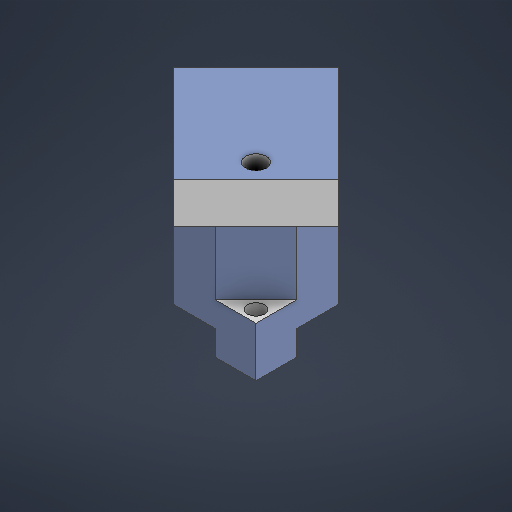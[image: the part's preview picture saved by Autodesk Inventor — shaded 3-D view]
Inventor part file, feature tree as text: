
AUTODESK INVENTOR PART (.ipt)
format: ipt  version: 2025.1 (Build 291241000, 241)  size: 527,360 bytes
history: native  units: in
note: dims shown in document units (in); Inventor stores cm internally (conversion verified against a paired STEP export)
features: extrude x10, sketch x10, projected_geometry x1, other x1
ambient origin geometry x8: Origin, YZ Plane, XZ Plane, XY Plane, X Axis, Y Axis, Z Axis, Center Point
bodies: Solid1 (feature_tree)
feature tree (22):
  extrude  "Extrusion1"  Depth=0.1949in
  extrude  "Extrusion2"  Depth=0.3937in
  extrude  "Extrusion3"  Depth=0.3937in TaperAngle=0.0deg
  extrude  "Extrusion4"  Depth=0.1969in TaperAngle=0.0deg
  extrude  "Extrusion5"  Depth=0.1969in TaperAngle=0.0deg
  extrude  "Extrusion6"  Depth=0.1299in
  extrude  "Extrusion7"  Depth=0.105in
  extrude  "Extrusion8"  Depth=0.0571in
  extrude  "Extrusion9"  Depth=0.3937in TaperAngle=0.0deg
  extrude  "Extrusion10"  Depth=0.6496in
  sketch  "Sketch1"  dims[d0=0.1949in d1=0.1949in]
  sketch  "Sketch2"  dims[d2=0.2362in d3=0.0in d4=0.3937in]
  sketch  "Sketch3"  dims[d5=0.3937in d6=0.0787in d7=0.0in]
  sketch  "Sketch4"  dims[d8=0.7776in d9=0.0in d10=0.1969in d11=0.0in]
  sketch  "Sketch6"  dims[d12=0.0984in d13=0.1969in d14=0.0in]
  sketch  "Sketch7"  dims[d15=0.0787in d16=0.0in d17=0.1299in]
  sketch  "Sketch8"  dims[d18=0.105in d19=0.105in]
  sketch  "Sketch9"  dims[d20=0.0571in d21=0.0571in]
  sketch  "Sketch10"  dims[d22=0.0787in d23=0.3937in d24=0.0in]
  projected_geometry  "Projected Loop1"
  sketch  "Sketch11"  dims[d25=45.0deg d26=0.6496in d27=135.0deg d28=0.1969in d29=0.0984in d30=0.3937in d31=0.0in d32=0.1181in d33=0.0in d34=0.1575in d35=0.0in]
  other  "Finish1"
